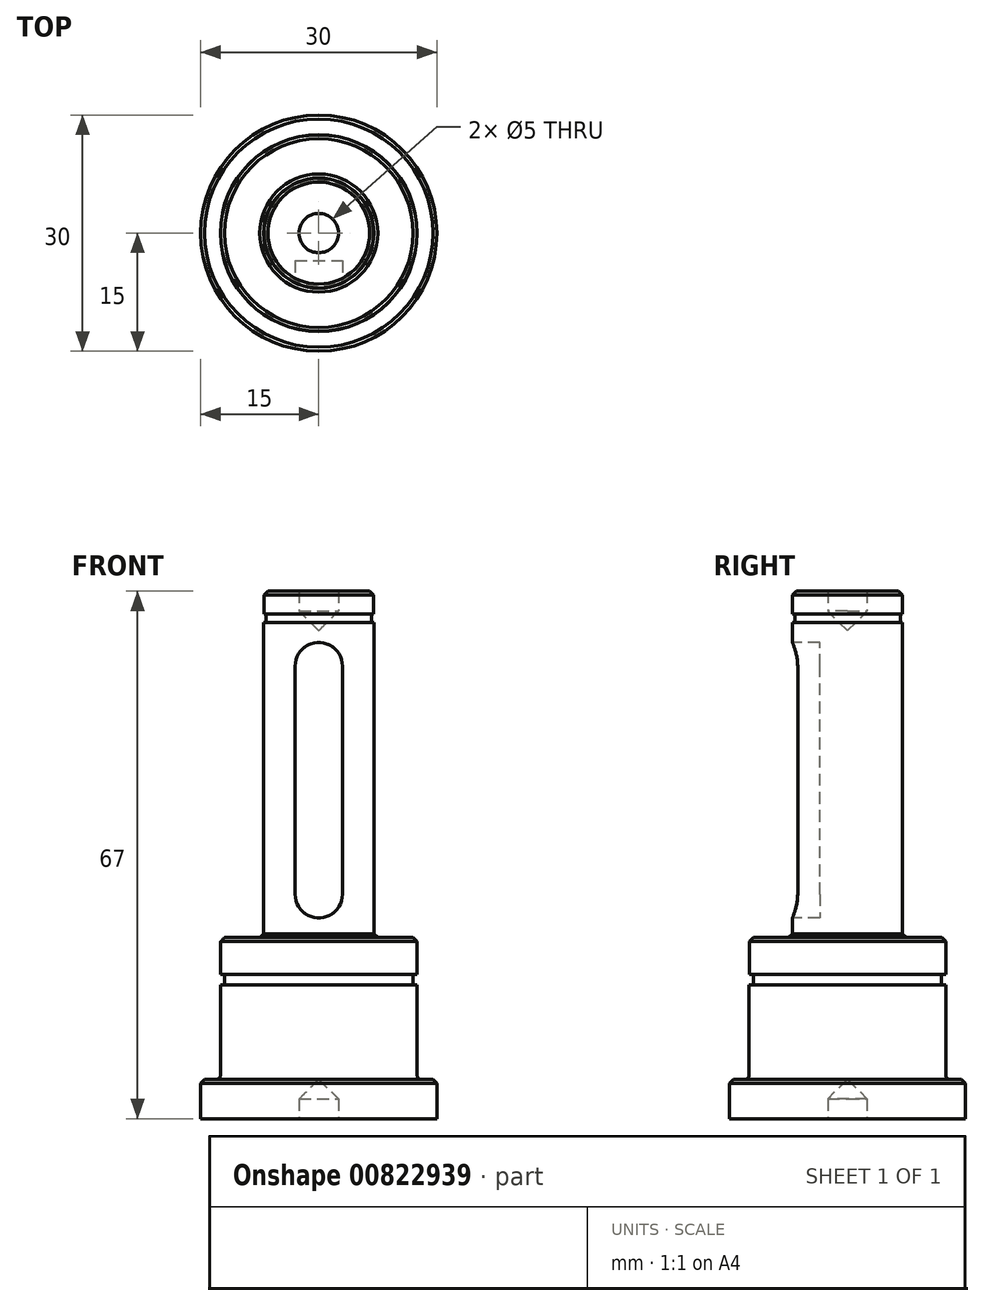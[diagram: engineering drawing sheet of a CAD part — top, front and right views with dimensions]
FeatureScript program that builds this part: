
annotation { "Feature Type Name" : "Feature", "Feature Type Description" : "" }
export const myFeature = defineFeature(function(context is Context, id is Id, definition is map)
    precondition{}
    {
        {
            var Q0;
            Q0=qCreatedBy(makeId("Front.planeOp"),FACE);
            var sketch = newSketch(context, id + "F0", { "sketchPlane" : qUnion([Q0])});
            skLineSegment(sketch, "E0", {"start": v(0, 0) * mm, "end": v(0, 15) * mm});
            skLineSegment(sketch, "E1", {"start": v(0, 15) * mm, "end": v(2.5, 17.5) * mm});
            skLineSegment(sketch, "E2", {"start": v(2.5, 17.5) * mm, "end": v(2.5, 20) * mm});
            skLineSegment(sketch, "E3", {"start": v(2.5, 20) * mm, "end": v(6.98, 20) * mm});
            skLineSegment(sketch, "E4", {"start": v(6.98, 20) * mm, "end": v(6.98, 17.1) * mm});
            skLineSegment(sketch, "E5", {"start": v(6.98, 17.1) * mm, "end": v(6.7, 17.1) * mm});
            skLineSegment(sketch, "E6", {"start": v(6.7, 17.1) * mm, "end": v(6.7, 16) * mm});
            skLineSegment(sketch, "E7", {"start": v(6.7, 16) * mm, "end": v(7, 16) * mm});
            skLineSegment(sketch, "E8", {"start": v(7, 16) * mm, "end": v(7, -24) * mm});
            skLineSegment(sketch, "E9", {"start": v(7, -24) * mm, "end": v(12.48, -24) * mm});
            skLineSegment(sketch, "E10", {"start": v(12.48, -24) * mm, "end": v(12.48, -28.7) * mm});
            skLineSegment(sketch, "E11", {"start": v(12.48, -28.7) * mm, "end": v(11.95, -28.7) * mm});
            skLineSegment(sketch, "E12", {"start": v(11.95, -28.7) * mm, "end": v(11.95, -30) * mm});
            skLineSegment(sketch, "E13", {"start": v(11.95, -30) * mm, "end": v(12.5, -30) * mm});
            skLineSegment(sketch, "E14", {"start": v(12.5, -30) * mm, "end": v(12.5, -42) * mm});
            skLineSegment(sketch, "E15", {"start": v(12.5, -42) * mm, "end": v(15, -42) * mm});
            skLineSegment(sketch, "E16", {"start": v(15, -42) * mm, "end": v(15, -45) * mm});
            skLineSegment(sketch, "E17", {"start": v(15, -45) * mm, "end": v(15, -45) * mm});
            skLineSegment(sketch, "E18", {"start": v(15, -45) * mm, "end": v(15, -47) * mm});
            skLineSegment(sketch, "E19", {"start": v(2.5, -47) * mm, "end": v(2.5, -44.5) * mm});
            skLineSegment(sketch, "E20", {"start": v(2.5, -44.5) * mm, "end": v(0, -42) * mm});
            skLineSegment(sketch, "E21", {"start": v(0, -42) * mm, "end": v(0, 0) * mm});
            skLineSegment(sketch, "E22", {"start": v(15, -47) * mm, "end": v(2.5, -47) * mm});
            skLineSegment(sketch, "E23", {"start": v(0, 15) * mm, "end": v(0, 95.93) * mm, "construction": true});
            skLineSegment(sketch, "E24", {"start": v(0, -42) * mm, "end": v(0, -104.42) * mm, "construction": true});
            skSolve(sketch);
        }
        {
            var Q0;
            Q0=qSketchRegion(id+"F0",true);
            var Q1;
            Q1=sQuery(id+"F0.wireOp",EDGE,"E23");
            revolve(context, id + "F1", {"surfaceOperationType" : NewSurfaceOperationType.NEW, "entities" : qUnion([Q0]), "axis" : qUnion([Q1]), "revolveType" : RevolveType.FULL});
        }
        {
            var Q0;
            Q0=makeQuery(id+"F1.opRevolve","SWEPT_EDGE",EDGE,{"disambiguationData":[OSD([sQuery(id+"F0.wireOp",EDGE,"E3"),sQuery(id+"F0.wireOp",EDGE,"E4")])]});
            var Q1;
            Q1=makeQuery(id+"F1.opRevolve","SWEPT_FACE",FACE,{"disambiguationData":[OSD([sQuery(id+"F0.wireOp",EDGE,"E9")])]});
            var Q2;
            Q2=makeQuery(id+"F1.opRevolve","SWEPT_EDGE",EDGE,{"disambiguationData":[OSD([sQuery(id+"F0.wireOp",EDGE,"E15"),sQuery(id+"F0.wireOp",EDGE,"E16")])]});
            chamfer(context, id + "F2", {"entities" : qUnion([Q0, Q1, Q2]), "width" : 0.5 * mm, "tangentPropagation" : true});
        }
        {
            var Q0;
            Q0=makeQuery(id+"F1.opRevolve","SWEPT_EDGE",EDGE,{"disambiguationData":[OSD([sQuery(id+"F0.wireOp",EDGE,"E14"),sQuery(id+"F0.wireOp",EDGE,"E15")])]});
            fillet(context, id + "F3", {"entities" : qUnion([Q0]), "radius" : 0.5 * mm, "tangentPropagation" : true, "allowEdgeOverflow" : false});
        }
        {
            var Q0;
            Q0=qCreatedBy(makeId("Front.planeOp"),FACE);
            cPlane(context, id + "F4", {"entities" : qUnion([Q0]), "cplaneType" : CPlaneType.OFFSET, "offset" : 7 * mm, "width" : 150 * mm, "height" : 150 * mm});
        }
        {
            var Q0;
            Q0=qCreatedBy(id+"F4.planeOp",FACE);
            var sketch = newSketch(context, id + "F5", { "sketchPlane" : qUnion([Q0])});
            skLineSegment(sketch, "E25", {"start": v(0, 0) * mm, "end": v(0, 10.5) * mm, "construction": true});
            skLineSegment(sketch, "E26", {"start": v(0, -18.5) * mm, "end": v(0, 0) * mm, "construction": true});
            skArc(sketch, "E27", {"start": v(3, 10.5) * mm, "mid": v(0, 13.5) * mm, "end": v(-3, 10.5) * mm});
            skArc(sketch, "E28", {"start": v(-3, -18.5) * mm, "mid": v(0, -21.5) * mm, "end": v(3, -18.5) * mm});
            skLineSegment(sketch, "E29.0", {"start": v(7, 16) * mm, "end": v(-7, 16) * mm, "construction": true});
            skLineSegment(sketch, "E29.1", {"start": v(-11.98, -24) * mm, "end": v(11.98, -24) * mm, "construction": true});
            skLineSegment(sketch, "E30", {"start": v(3, -18.5) * mm, "end": v(3, 10.5) * mm});
            skLineSegment(sketch, "E31", {"start": v(-3, 10.5) * mm, "end": v(-3, -18.5) * mm});
            skSolve(sketch);
        }
        {
            var Q0;
            Q0=qSketchRegion(id+"F5",true);
            extrude(context, id + "F6", {"entities" : qUnion([Q0]), "operationType" : NewBodyOperationType.REMOVE, "oppositeDirection" : true, "depth" : 3.5 * mm, "offsetDistance" : 25 * mm});
        }
    });
